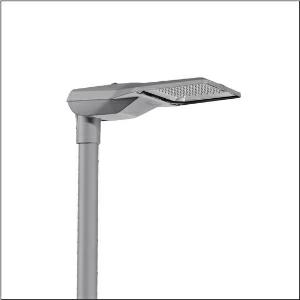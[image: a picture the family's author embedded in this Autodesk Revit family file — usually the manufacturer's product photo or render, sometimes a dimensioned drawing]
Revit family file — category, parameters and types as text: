
# Revit family: streetlight_sl_21_iq_midi___st1_0ab_5xe3m31v08nb_f534
name_source: partatom
category: Lighting Fixtures
units: mm (PartAtom-declared; Revit-internal decimal feet)

## family parameters
Cut with Voids When Loaded = No
Host = Face
Light Source = No
Part Type = Normal
Room Calculation Point = No
Round Connector Dimension = Use Diameter
Shared = No

## types (1)
- --- (1 x LED, 18970 lm, 136.6 W, 3000K)
    Apparent Load = 137 VA
    CIE Flux Codes = 40 74 97 100 100
    Color Rendering = 70
    Color Temperature = 3000K
    Default Elevation = 1800 mm
    Description = Streetlight SL 21 iQ midi, mast luminaire, primary light control with lens, of PMMA, primary optical cover: cover, of toughened safety glass, transparent, light distribution: ST1.0aB, light emission: direct distribution, primary light characteristic: asymmetric, installation type: post-top, side-entry, LED, High Power LED, rated luminous flux: 18.970lm, luminous efficacy: 139lm/W, light colour: 730, colour temperature: 3000K, control: pre-setting: logarithmic dimming characteristic, Street-Remote, Auto-Match, Temp-Guard, Lumen-Switch, Night-Set, Smart-Wire, Light-Fading, Desk-Remote (wireless, voltage-free reading and setting of iQ features in the workshop via application-optimized NFC function/RFID function), optimised constant luminous flux control (CLO 2.0), mains connection: 230..240V, AC, 50/60Hz, start of lifetime: 137W, end of service life: 144W, reduction: 61W, luminaire housing, of diecast aluminium, powder-coated, Siteco® metallic grey (DB 702S), corrosivity category C5 mid according to DIN EN ISO 12944, please order mast flange separately, inclination adjustable: 0°, 5°, 10°, 15°, sealing non-destructively replaceable, multi-level sealing system, length: 644mm, width: 335mm, height: 110mm, mast flange for spigot size: 42mm (side-entry): 5XC10008XM4, 60/48mm (side-entry/post-top): 5XC10108XM2, 76/60mm (side-entry/post-top): 5XC10108XM1, Smart Interface above, protection rating (complete): IP66, insulation class (complete): insulation class II (safety insulation), certification: CE, ENEC, ENEC+, VDE, impact resistance: IK09, permissible operating ambient temperature for outdoor applications: -40..+50°C, standard-compliant lighting for roads and squares, packaging unit: 1 piece

Light Distribution: ST1.0aB
    Height = 111 mm
    Lamp = 1 x LED
    Lamp Light Flux = 18970 lm
    Lamp Power = 136.6 W
    Lamp count = 1
    Length = 644 mm
    Luminous efficacy = 139 lm/W
    Manufacturer = Siteco
    ModVariant = No
    Model = 5XE3M31V08NB
    Number of Poles = 1
    OnlyDefault = Yes
    Power Factor = 1
    Product Name = Streetlight SL 21 iQ midi | ST1.0aB
    Product group = mast luminaire | pylon top
    ProductGroupID = 6100
    Protection Class = Protection class II
    Protection Degree = IP 66
    RLX_Detail_Level = 1
    RLX_Emergency_Light_Flux = 0 lm
    RLX_Emergency_Type = 0
    RLX_Emergency_Type_DB = No
    RlxData = <blob elided: 90837 chars, md5=291eb465>
    Socket = socket
    Standby Power = 0 W
    System Light Flux = 18970 lm
    System Power = 137 W
    Type Comments = factory setting: luminous flux: 100 % | dim-lin: 254 | 733 mA
    Type Image = l_1004302.jpg
    URL = http://relux.com
    VarID = @adj_080943
    Voltage = 0 V
    Weight = 0.00 kg
    Width = 336 mm

## geometry (parser evidence)
native form markers: Blend x4, Sweep x12
no freeform markers — native parametric forms only
